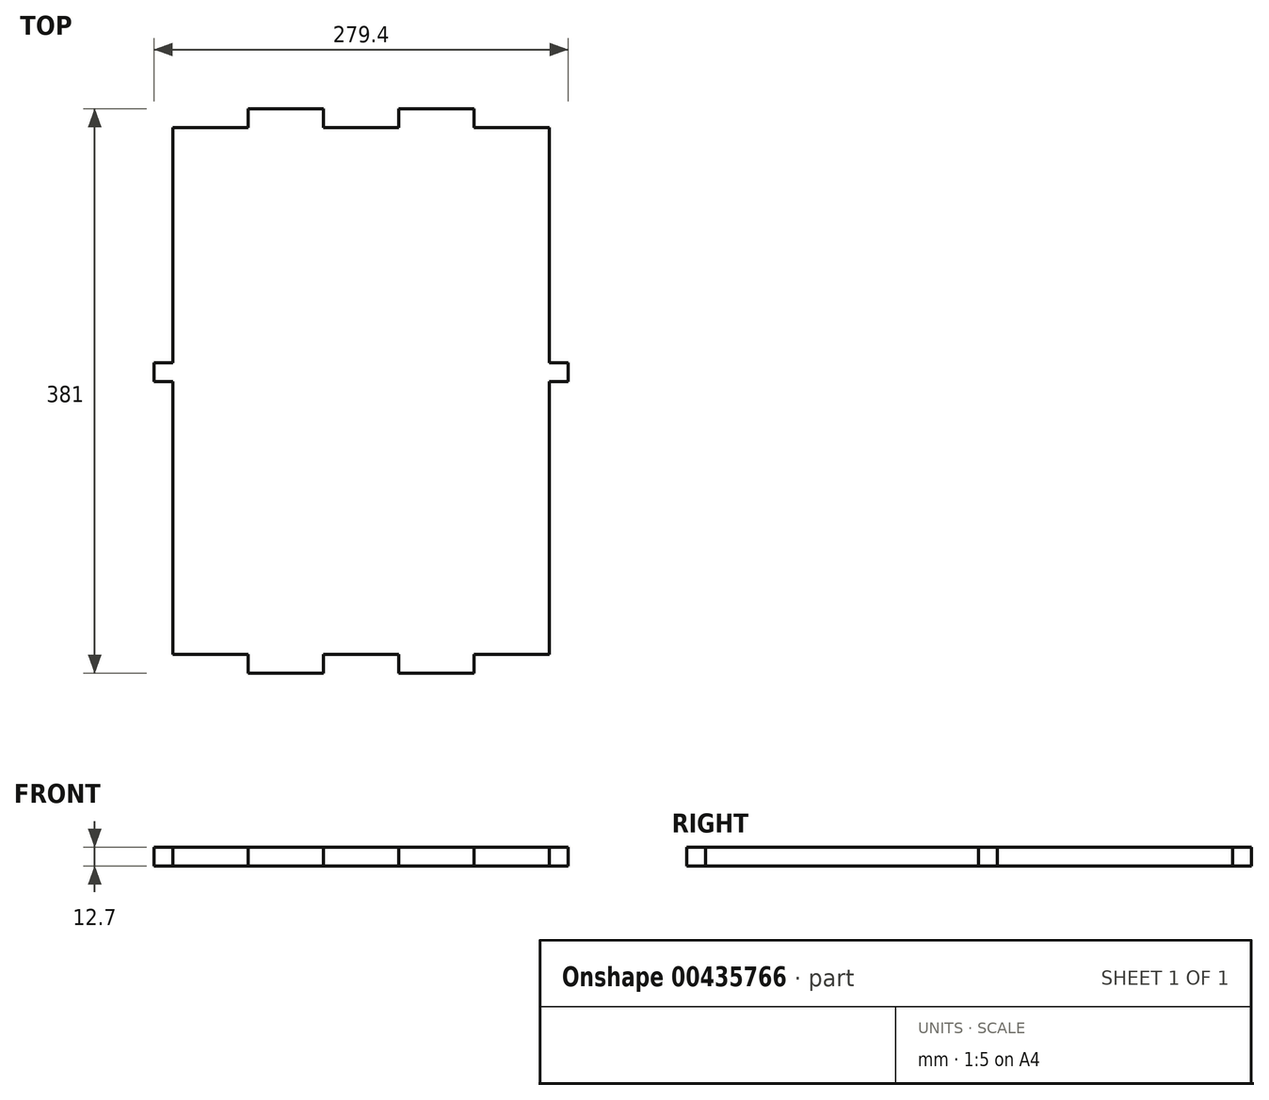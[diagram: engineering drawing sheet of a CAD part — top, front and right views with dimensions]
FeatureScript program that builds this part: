
annotation { "Feature Type Name" : "Feature", "Feature Type Description" : "" }
export const myFeature = defineFeature(function(context is Context, id is Id, definition is map)
    precondition{}
    {
        {
            var Q0;
            Q0=qCreatedBy(makeId("Top.planeOp"),FACE);
            var sketch = newSketch(context, id + "F0", { "sketchPlane" : qUnion([Q0])});
            skLineSegment(sketch, "E0.bottom", {"start": v(-76.2, 12.7) * mm, "end": v(-25.4, 12.7) * mm});
            skLineSegment(sketch, "E0.top", {"start": v(-76.2, -368.3) * mm, "end": v(-25.4, -368.3) * mm});
            skLineSegment(sketch, "E0.left", {"start": v(-127, 0) * mm, "end": v(-127, -158.75) * mm});
            skLineSegment(sketch, "E0.right", {"start": v(127, 0) * mm, "end": v(127, -158.75) * mm});
            skLineSegment(sketch, "E1", {"start": v(-127, 0) * mm, "end": v(-76.2, 0) * mm});
            skLineSegment(sketch, "E2", {"start": v(-76.2, 0) * mm, "end": v(-76.2, 12.7) * mm});
            skLineSegment(sketch, "E3", {"start": v(-25.4, 12.7) * mm, "end": v(-25.4, 0) * mm});
            skLineSegment(sketch, "E4", {"start": v(-25.4, 0) * mm, "end": v(25.4, 0) * mm});
            skLineSegment(sketch, "E5", {"start": v(25.4, 0) * mm, "end": v(25.4, 12.7) * mm});
            skLineSegment(sketch, "E6", {"start": v(76.2, 12.7) * mm, "end": v(76.2, 0) * mm});
            skLineSegment(sketch, "E7", {"start": v(76.2, 0) * mm, "end": v(127, 0) * mm});
            skPoint(sketch, "E8.orphan", {"position": v(-127, 12.7) * mm});
            skLineSegment(sketch, "E9.trimOffspring", {"start": v(25.4, 12.7) * mm, "end": v(76.2, 12.7) * mm});
            skLineSegment(sketch, "E10", {"start": v(-127, -355.6) * mm, "end": v(-76.2, -355.6) * mm});
            skLineSegment(sketch, "E11", {"start": v(-76.2, -355.6) * mm, "end": v(-76.2, -368.3) * mm});
            skLineSegment(sketch, "E12", {"start": v(-25.4, -368.3) * mm, "end": v(-25.4, -355.6) * mm});
            skLineSegment(sketch, "E13", {"start": v(-25.4, -355.6) * mm, "end": v(25.4, -355.6) * mm});
            skLineSegment(sketch, "E14", {"start": v(25.4, -355.6) * mm, "end": v(25.4, -368.3) * mm});
            skLineSegment(sketch, "E15", {"start": v(76.2, -368.3) * mm, "end": v(76.2, -355.6) * mm});
            skLineSegment(sketch, "E16", {"start": v(76.2, -355.6) * mm, "end": v(127, -355.6) * mm});
            skPoint(sketch, "E17.orphan", {"position": v(-127, -368.3) * mm});
            skLineSegment(sketch, "E18.trimOffspring", {"start": v(25.4, -368.3) * mm, "end": v(76.2, -368.3) * mm});
            skLineSegment(sketch, "E19", {"start": v(127, -158.75) * mm, "end": v(139.7, -158.75) * mm});
            skLineSegment(sketch, "E20", {"start": v(139.7, -158.75) * mm, "end": v(139.7, -171.45) * mm});
            skLineSegment(sketch, "E21", {"start": v(139.7, -171.45) * mm, "end": v(127, -171.45) * mm});
            skLineSegment(sketch, "E22", {"start": v(-127, -158.75) * mm, "end": v(-139.7, -158.75) * mm});
            skLineSegment(sketch, "E23", {"start": v(-139.7, -158.75) * mm, "end": v(-139.7, -171.45) * mm});
            skLineSegment(sketch, "E24", {"start": v(-139.7, -171.45) * mm, "end": v(-127, -171.45) * mm});
            skLineSegment(sketch, "E25.trimOffspring", {"start": v(-127, -171.45) * mm, "end": v(-127, -355.6) * mm});
            skLineSegment(sketch, "E26.trimOffspring", {"start": v(127, -171.45) * mm, "end": v(127, -355.6) * mm});
            skPoint(sketch, "E27", {"position": v(0, 0) * mm});
            skPoint(sketch, "E28", {"position": v(0, -177.8) * mm});
            skSolve(sketch);
        }
        {
            var Q0;
            Q0=makeQuery(id+"F0.imprint","IMPRINT",FACE,{"disambiguationData":[TD([[makeQuery(id+"F0.imprint","IMPRINT",EDGE,{"derivedFrom":sQuery(id+"F0.wireOp",EDGE,"E0.bottom")}),-1.0]])]});
            extrude(context, id + "F1", {"entities" : qUnion([Q0]), "depth" : 12.7 * mm});
        }
    });
